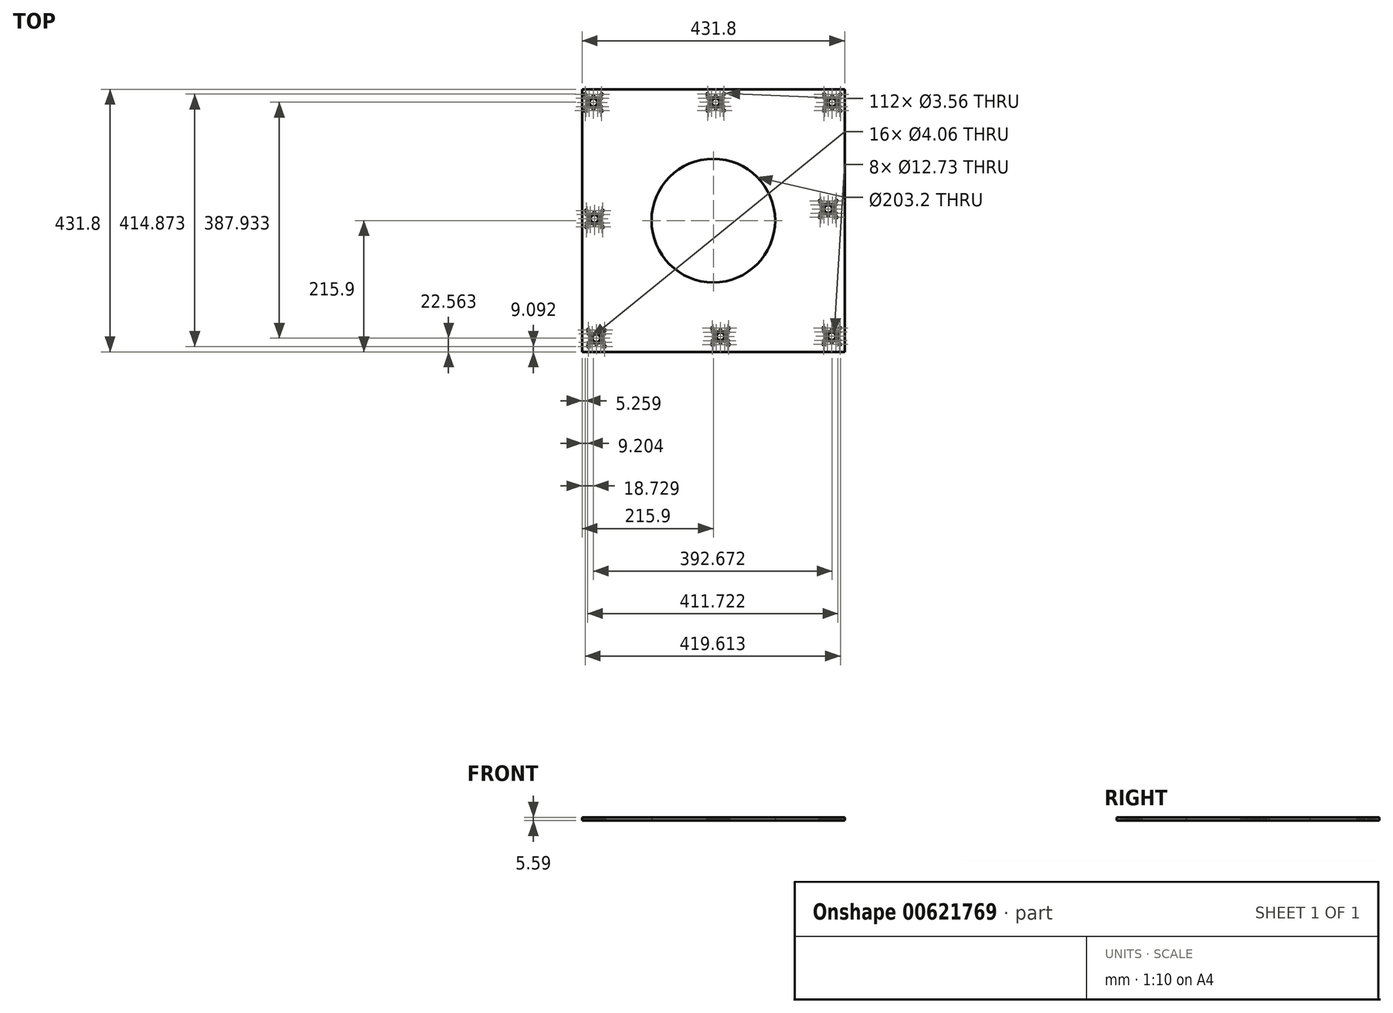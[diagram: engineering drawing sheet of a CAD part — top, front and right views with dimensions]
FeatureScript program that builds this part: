
annotation { "Feature Type Name" : "Feature", "Feature Type Description" : "" }
export const myFeature = defineFeature(function(context is Context, id is Id, definition is map)
    precondition{}
    {
        {
            var Q0;
            Q0=qCreatedBy(makeId("Top.planeOp"),FACE);
            var sketch = newSketch(context, id + "F0", { "sketchPlane" : qUnion([Q0])});
            skLineSegment(sketch, "E0.bottom", {"start": v(215.9, 215.9) * mm, "end": v(-215.9, 215.9) * mm});
            skLineSegment(sketch, "E0.top", {"start": v(215.9, -215.9) * mm, "end": v(-215.9, -215.9) * mm});
            skLineSegment(sketch, "E0.left", {"start": v(215.9, 215.9) * mm, "end": v(215.9, -215.9) * mm});
            skLineSegment(sketch, "E0.right", {"start": v(-215.9, 215.9) * mm, "end": v(-215.9, -215.9) * mm});
            skPoint(sketch, "E0.middle", {"position": v(0, 0) * mm});
            skCircle(sketch, "E1", {"center": v(-197.17, 203.97) * mm, "radius": 1.78 * mm});
            skPoint(sketch, "E1.first.point", {"position": v(-197.12, 205.75) * mm});
            skPoint(sketch, "E1.second.point", {"position": v(-196.95, 202.2) * mm});
            skPoint(sketch, "E1.third.point", {"position": v(-198.95, 203.93) * mm});
            skCircle(sketch, "E2", {"center": v(-197.17, 184.41) * mm, "radius": 1.78 * mm});
            skPoint(sketch, "E2.first.point", {"position": v(-197.01, 182.64) * mm});
            skPoint(sketch, "E2.second.point", {"position": v(-195.97, 185.72) * mm});
            skPoint(sketch, "E2.third.point", {"position": v(-197.85, 186.05) * mm});
            skPoint(sketch, "E3.first.point", {"position": v(-203.33, 179.04) * mm});
            skPoint(sketch, "E3.second.point", {"position": v(-201.5, 181.99) * mm});
            skPoint(sketch, "E3.third.point", {"position": v(-204.3, 181.6) * mm});
            skPoint(sketch, "E4.first.point", {"position": v(-190.35, 179.44) * mm});
            skPoint(sketch, "E4.second.point", {"position": v(-191.53, 182.5) * mm});
            skPoint(sketch, "E4.third.point", {"position": v(-193.13, 179.84) * mm});
            skPoint(sketch, "E5.first.point", {"position": v(-191.34, 205.9) * mm});
            skPoint(sketch, "E5.second.point", {"position": v(-191.37, 209.42) * mm});
            skPoint(sketch, "E5.third.point", {"position": v(-193.33, 207.3) * mm});
            skPoint(sketch, "E6.first.point", {"position": v(-204.43, 207.08) * mm});
            skPoint(sketch, "E6.second.point", {"position": v(-201.44, 208.86) * mm});
            skPoint(sketch, "E6.third.point", {"position": v(-203.63, 209.2) * mm});
            skCircle(sketch, "E7", {"center": v(-210.64, 207.66) * mm, "radius": 1.78 * mm});
            skPoint(sketch, "E7.first.point", {"position": v(-210.57, 209.44) * mm});
            skPoint(sketch, "E7.second.point", {"position": v(-209.71, 206.14) * mm});
            skPoint(sketch, "E7.third.point", {"position": v(-212.15, 206.72) * mm});
            skCircle(sketch, "E8", {"center": v(-183.7, 207.66) * mm, "radius": 1.78 * mm});
            skPoint(sketch, "E8.first.point", {"position": v(-183.2, 205.95) * mm});
            skPoint(sketch, "E8.second.point", {"position": v(-183.5, 209.43) * mm});
            skPoint(sketch, "E8.third.point", {"position": v(-185.46, 207.43) * mm});
            skCircle(sketch, "E9", {"center": v(-185.04, 201.1) * mm, "radius": 1.78 * mm});
            skPoint(sketch, "E9.first.point", {"position": v(-184.76, 202.86) * mm});
            skPoint(sketch, "E9.second.point", {"position": v(-185, 199.33) * mm});
            skPoint(sketch, "E9.third.point", {"position": v(-186, 202.6) * mm});
            skCircle(sketch, "E10", {"center": v(-190.26, 201.1) * mm, "radius": 1.78 * mm});
            skPoint(sketch, "E10.first.point", {"position": v(-189.77, 199.4) * mm});
            skPoint(sketch, "E10.second.point", {"position": v(-190.12, 202.88) * mm});
            skPoint(sketch, "E10.third.point", {"position": v(-191.55, 202.32) * mm});
            skCircle(sketch, "E11", {"center": v(-204.09, 201.1) * mm, "radius": 1.78 * mm});
            skPoint(sketch, "E11.first.point", {"position": v(-204.41, 199.36) * mm});
            skPoint(sketch, "E11.second.point", {"position": v(-202.41, 201.7) * mm});
            skPoint(sketch, "E11.third.point", {"position": v(-204.37, 202.86) * mm});
            skCircle(sketch, "E12", {"center": v(-209.3, 201.1) * mm, "radius": 1.78 * mm});
            skPoint(sketch, "E12.first.point", {"position": v(-209.27, 199.33) * mm});
            skPoint(sketch, "E12.second.point", {"position": v(-208.54, 202.7) * mm});
            skPoint(sketch, "E12.third.point", {"position": v(-209.18, 202.88) * mm});
            skCircle(sketch, "E13", {"center": v(-206.7, 194.19) * mm, "radius": 2.03 * mm});
            skPoint(sketch, "E13.first.point", {"position": v(-205.34, 195.7) * mm});
            skPoint(sketch, "E13.second.point", {"position": v(-205.21, 192.8) * mm});
            skPoint(sketch, "E13.third.point", {"position": v(-208.45, 195.21) * mm});
            skCircle(sketch, "E14", {"center": v(-197.17, 194.19) * mm, "radius": 6.36 * mm});
            skPoint(sketch, "E14.first.point", {"position": v(-198.39, 187.94) * mm});
            skPoint(sketch, "E14.second.point", {"position": v(-191.45, 196.97) * mm});
            skPoint(sketch, "E14.third.point", {"position": v(-201.2, 199.12) * mm});
            skCircle(sketch, "E15", {"center": v(-187.65, 194.19) * mm, "radius": 2.03 * mm});
            skPoint(sketch, "E15.first.point", {"position": v(-187.5, 192.16) * mm});
            skPoint(sketch, "E15.second.point", {"position": v(-186.02, 195.4) * mm});
            skPoint(sketch, "E15.third.point", {"position": v(-188.05, 196.18) * mm});
            skCircle(sketch, "E16", {"center": v(-185.04, 187.27) * mm, "radius": 1.78 * mm});
            skPoint(sketch, "E16.first.point", {"position": v(-184.91, 185.5) * mm});
            skPoint(sketch, "E16.second.point", {"position": v(-183.5, 188.16) * mm});
            skPoint(sketch, "E16.third.point", {"position": v(-186.23, 188.6) * mm});
            skCircle(sketch, "E17", {"center": v(-190.26, 187.27) * mm, "radius": 1.78 * mm});
            skPoint(sketch, "E17.first.point", {"position": v(-190.37, 185.5) * mm});
            skPoint(sketch, "E17.second.point", {"position": v(-189.35, 188.8) * mm});
            skPoint(sketch, "E17.third.point", {"position": v(-191.13, 188.82) * mm});
            skCircle(sketch, "E18", {"center": v(-183.7, 180.72) * mm, "radius": 1.78 * mm});
            skPoint(sketch, "E18.first.point", {"position": v(-184.91, 179.42) * mm});
            skPoint(sketch, "E18.second.point", {"position": v(-182.65, 182.16) * mm});
            skPoint(sketch, "E18.third.point", {"position": v(-182.59, 179.33) * mm});
            skCircle(sketch, "E19", {"center": v(-210.64, 180.72) * mm, "radius": 1.78 * mm});
            skPoint(sketch, "E19.first.point", {"position": v(-211.22, 179.04) * mm});
            skPoint(sketch, "E19.second.point", {"position": v(-209.26, 181.84) * mm});
            skPoint(sketch, "E19.third.point", {"position": v(-211.92, 181.96) * mm});
            skCircle(sketch, "E20", {"center": v(-209.3, 187.27) * mm, "radius": 1.78 * mm});
            skPoint(sketch, "E20.first.point", {"position": v(-209.7, 185.54) * mm});
            skPoint(sketch, "E20.second.point", {"position": v(-208.08, 188.56) * mm});
            skPoint(sketch, "E20.third.point", {"position": v(-209.79, 188.99) * mm});
            skCircle(sketch, "E21", {"center": v(-204.09, 187.27) * mm, "radius": 1.78 * mm});
            skPoint(sketch, "E21.first.point", {"position": v(-204.51, 185.55) * mm});
            skPoint(sketch, "E21.second.point", {"position": v(-203.33, 188.88) * mm});
            skPoint(sketch, "E21.third.point", {"position": v(-205.24, 188.62) * mm});
            skCircle(sketch, "E22", {"center": v(195.5, 203.97) * mm, "radius": 1.78 * mm});
            skPoint(sketch, "E22.first.point", {"position": v(195.55, 205.75) * mm});
            skPoint(sketch, "E22.second.point", {"position": v(195.72, 202.2) * mm});
            skPoint(sketch, "E22.third.point", {"position": v(193.72, 203.93) * mm});
            skCircle(sketch, "E23", {"center": v(195.5, 184.41) * mm, "radius": 1.78 * mm});
            skPoint(sketch, "E23.first.point", {"position": v(195.66, 182.64) * mm});
            skPoint(sketch, "E23.second.point", {"position": v(196.7, 185.72) * mm});
            skPoint(sketch, "E23.third.point", {"position": v(194.82, 186.05) * mm});
            skPoint(sketch, "E24.first.point", {"position": v(189.34, 179.04) * mm});
            skPoint(sketch, "E24.second.point", {"position": v(191.17, 181.99) * mm});
            skPoint(sketch, "E24.third.point", {"position": v(188.38, 181.6) * mm});
            skPoint(sketch, "E25.first.point", {"position": v(202.32, 179.44) * mm});
            skPoint(sketch, "E25.second.point", {"position": v(201.14, 182.5) * mm});
            skPoint(sketch, "E25.third.point", {"position": v(199.54, 179.84) * mm});
            skPoint(sketch, "E26.first.point", {"position": v(201.33, 205.9) * mm});
            skPoint(sketch, "E26.second.point", {"position": v(201.3, 209.42) * mm});
            skPoint(sketch, "E26.third.point", {"position": v(199.34, 207.3) * mm});
            skPoint(sketch, "E27.first.point", {"position": v(188.24, 207.08) * mm});
            skPoint(sketch, "E27.second.point", {"position": v(191.23, 208.86) * mm});
            skPoint(sketch, "E27.third.point", {"position": v(189.04, 209.2) * mm});
            skCircle(sketch, "E28", {"center": v(182.03, 207.66) * mm, "radius": 1.78 * mm});
            skPoint(sketch, "E28.first.point", {"position": v(182.1, 209.44) * mm});
            skPoint(sketch, "E28.second.point", {"position": v(182.96, 206.14) * mm});
            skPoint(sketch, "E28.third.point", {"position": v(180.52, 206.72) * mm});
            skCircle(sketch, "E29", {"center": v(208.97, 207.66) * mm, "radius": 1.78 * mm});
            skPoint(sketch, "E29.first.point", {"position": v(209.47, 205.95) * mm});
            skPoint(sketch, "E29.second.point", {"position": v(209.18, 209.43) * mm});
            skPoint(sketch, "E29.third.point", {"position": v(207.2, 207.43) * mm});
            skCircle(sketch, "E30", {"center": v(207.64, 201.1) * mm, "radius": 1.78 * mm});
            skPoint(sketch, "E30.first.point", {"position": v(207.92, 202.86) * mm});
            skPoint(sketch, "E30.second.point", {"position": v(207.67, 199.33) * mm});
            skPoint(sketch, "E30.third.point", {"position": v(206.66, 202.6) * mm});
            skCircle(sketch, "E31", {"center": v(202.42, 201.1) * mm, "radius": 1.78 * mm});
            skPoint(sketch, "E31.first.point", {"position": v(202.9, 199.4) * mm});
            skPoint(sketch, "E31.second.point", {"position": v(202.56, 202.88) * mm});
            skPoint(sketch, "E31.third.point", {"position": v(201.12, 202.32) * mm});
            skCircle(sketch, "E32", {"center": v(188.59, 201.1) * mm, "radius": 1.78 * mm});
            skPoint(sketch, "E32.first.point", {"position": v(188.26, 199.36) * mm});
            skPoint(sketch, "E32.second.point", {"position": v(190.26, 201.7) * mm});
            skPoint(sketch, "E32.third.point", {"position": v(188.3, 202.86) * mm});
            skCircle(sketch, "E33", {"center": v(183.37, 201.1) * mm, "radius": 1.78 * mm});
            skPoint(sketch, "E33.first.point", {"position": v(183.4, 199.33) * mm});
            skPoint(sketch, "E33.second.point", {"position": v(184.14, 202.7) * mm});
            skPoint(sketch, "E33.third.point", {"position": v(183.49, 202.88) * mm});
            skCircle(sketch, "E34", {"center": v(185.98, 194.19) * mm, "radius": 2.03 * mm});
            skPoint(sketch, "E34.first.point", {"position": v(187.34, 195.7) * mm});
            skPoint(sketch, "E34.second.point", {"position": v(187.46, 192.8) * mm});
            skPoint(sketch, "E34.third.point", {"position": v(184.22, 195.21) * mm});
            skCircle(sketch, "E35", {"center": v(195.5, 194.19) * mm, "radius": 6.36 * mm});
            skPoint(sketch, "E35.first.point", {"position": v(194.29, 187.94) * mm});
            skPoint(sketch, "E35.second.point", {"position": v(201.22, 196.97) * mm});
            skPoint(sketch, "E35.third.point", {"position": v(191.48, 199.12) * mm});
            skCircle(sketch, "E36", {"center": v(205.03, 194.19) * mm, "radius": 2.03 * mm});
            skPoint(sketch, "E36.first.point", {"position": v(205.17, 192.16) * mm});
            skPoint(sketch, "E36.second.point", {"position": v(206.65, 195.4) * mm});
            skPoint(sketch, "E36.third.point", {"position": v(204.62, 196.18) * mm});
            skCircle(sketch, "E37", {"center": v(207.64, 187.27) * mm, "radius": 1.78 * mm});
            skPoint(sketch, "E37.first.point", {"position": v(207.76, 185.5) * mm});
            skPoint(sketch, "E37.second.point", {"position": v(209.18, 188.16) * mm});
            skPoint(sketch, "E37.third.point", {"position": v(206.44, 188.6) * mm});
            skCircle(sketch, "E38", {"center": v(202.42, 187.27) * mm, "radius": 1.78 * mm});
            skPoint(sketch, "E38.first.point", {"position": v(202.3, 185.5) * mm});
            skPoint(sketch, "E38.second.point", {"position": v(203.33, 188.8) * mm});
            skPoint(sketch, "E38.third.point", {"position": v(201.54, 188.82) * mm});
            skCircle(sketch, "E39", {"center": v(208.97, 180.72) * mm, "radius": 1.78 * mm});
            skPoint(sketch, "E39.first.point", {"position": v(207.76, 179.42) * mm});
            skPoint(sketch, "E39.second.point", {"position": v(210.02, 182.16) * mm});
            skPoint(sketch, "E39.third.point", {"position": v(210.09, 179.33) * mm});
            skCircle(sketch, "E40", {"center": v(182.03, 180.72) * mm, "radius": 1.78 * mm});
            skPoint(sketch, "E40.first.point", {"position": v(181.45, 179.04) * mm});
            skPoint(sketch, "E40.second.point", {"position": v(183.41, 181.84) * mm});
            skPoint(sketch, "E40.third.point", {"position": v(180.76, 181.96) * mm});
            skCircle(sketch, "E41", {"center": v(183.37, 187.27) * mm, "radius": 1.78 * mm});
            skPoint(sketch, "E41.first.point", {"position": v(182.97, 185.54) * mm});
            skPoint(sketch, "E41.second.point", {"position": v(184.6, 188.56) * mm});
            skPoint(sketch, "E41.third.point", {"position": v(182.88, 188.99) * mm});
            skCircle(sketch, "E42", {"center": v(188.59, 187.27) * mm, "radius": 1.78 * mm});
            skPoint(sketch, "E42.first.point", {"position": v(188.16, 185.55) * mm});
            skPoint(sketch, "E42.second.point", {"position": v(189.34, 188.88) * mm});
            skPoint(sketch, "E42.third.point", {"position": v(187.43, 188.62) * mm});
            skCircle(sketch, "E43", {"center": v(3.89, 204.37) * mm, "radius": 1.78 * mm});
            skPoint(sketch, "E43.first.point", {"position": v(3.94, 206.15) * mm});
            skPoint(sketch, "E43.second.point", {"position": v(4.11, 202.6) * mm});
            skPoint(sketch, "E43.third.point", {"position": v(2.11, 204.33) * mm});
            skCircle(sketch, "E44", {"center": v(3.89, 184.82) * mm, "radius": 1.78 * mm});
            skPoint(sketch, "E44.first.point", {"position": v(4.05, 183.05) * mm});
            skPoint(sketch, "E44.second.point", {"position": v(5.1, 186.12) * mm});
            skPoint(sketch, "E44.third.point", {"position": v(3.2, 186.46) * mm});
            skPoint(sketch, "E45.first.point", {"position": v(-2.27, 179.44) * mm});
            skPoint(sketch, "E45.second.point", {"position": v(-0.45, 182.4) * mm});
            skPoint(sketch, "E45.third.point", {"position": v(-3.24, 182) * mm});
            skPoint(sketch, "E46.first.point", {"position": v(10.7, 179.85) * mm});
            skPoint(sketch, "E46.second.point", {"position": v(9.53, 182.9) * mm});
            skPoint(sketch, "E46.third.point", {"position": v(7.93, 180.24) * mm});
            skPoint(sketch, "E47.first.point", {"position": v(9.72, 206.3) * mm});
            skPoint(sketch, "E47.second.point", {"position": v(9.69, 209.83) * mm});
            skPoint(sketch, "E47.third.point", {"position": v(7.73, 207.7) * mm});
            skPoint(sketch, "E48.first.point", {"position": v(-3.37, 207.49) * mm});
            skPoint(sketch, "E48.second.point", {"position": v(-0.38, 209.27) * mm});
            skPoint(sketch, "E48.third.point", {"position": v(-2.57, 209.6) * mm});
            skCircle(sketch, "E49", {"center": v(-9.58, 208.07) * mm, "radius": 1.78 * mm});
            skPoint(sketch, "E49.first.point", {"position": v(-9.5, 209.84) * mm});
            skPoint(sketch, "E49.second.point", {"position": v(-8.65, 206.55) * mm});
            skPoint(sketch, "E49.third.point", {"position": v(-11.1, 207.13) * mm});
            skCircle(sketch, "E50", {"center": v(17.36, 208.07) * mm, "radius": 1.78 * mm});
            skPoint(sketch, "E50.first.point", {"position": v(17.86, 206.36) * mm});
            skPoint(sketch, "E50.second.point", {"position": v(17.56, 209.83) * mm});
            skPoint(sketch, "E50.third.point", {"position": v(15.6, 207.84) * mm});
            skCircle(sketch, "E51", {"center": v(16.02, 201.5) * mm, "radius": 1.78 * mm});
            skPoint(sketch, "E51.first.point", {"position": v(16.3, 203.27) * mm});
            skPoint(sketch, "E51.second.point", {"position": v(16.06, 199.73) * mm});
            skPoint(sketch, "E51.third.point", {"position": v(15.05, 203) * mm});
            skCircle(sketch, "E52", {"center": v(10.8, 201.5) * mm, "radius": 1.78 * mm});
            skPoint(sketch, "E52.first.point", {"position": v(11.3, 199.8) * mm});
            skPoint(sketch, "E52.second.point", {"position": v(10.94, 203.28) * mm});
            skPoint(sketch, "E52.third.point", {"position": v(9.51, 202.73) * mm});
            skCircle(sketch, "E53", {"center": v(-3.03, 201.5) * mm, "radius": 1.78 * mm});
            skPoint(sketch, "E53.first.point", {"position": v(-3.35, 199.76) * mm});
            skPoint(sketch, "E53.second.point", {"position": v(-1.35, 202.11) * mm});
            skPoint(sketch, "E53.third.point", {"position": v(-3.3, 203.27) * mm});
            skCircle(sketch, "E54", {"center": v(-8.25, 201.5) * mm, "radius": 1.78 * mm});
            skPoint(sketch, "E54.first.point", {"position": v(-8.21, 199.73) * mm});
            skPoint(sketch, "E54.second.point", {"position": v(-7.47, 203.11) * mm});
            skPoint(sketch, "E54.third.point", {"position": v(-8.12, 203.28) * mm});
            skCircle(sketch, "E55", {"center": v(-5.64, 194.6) * mm, "radius": 2.03 * mm});
            skPoint(sketch, "E55.first.point", {"position": v(-4.28, 196.1) * mm});
            skPoint(sketch, "E55.second.point", {"position": v(-4.15, 193.2) * mm});
            skPoint(sketch, "E55.third.point", {"position": v(-7.4, 195.62) * mm});
            skCircle(sketch, "E56", {"center": v(3.89, 194.6) * mm, "radius": 6.36 * mm});
            skPoint(sketch, "E56.first.point", {"position": v(2.67, 188.35) * mm});
            skPoint(sketch, "E56.second.point", {"position": v(9.61, 197.38) * mm});
            skPoint(sketch, "E56.third.point", {"position": v(-0.13, 199.53) * mm});
            skCircle(sketch, "E57", {"center": v(13.41, 194.6) * mm, "radius": 2.03 * mm});
            skPoint(sketch, "E57.first.point", {"position": v(13.56, 192.57) * mm});
            skPoint(sketch, "E57.second.point", {"position": v(15.04, 195.81) * mm});
            skPoint(sketch, "E57.third.point", {"position": v(13.01, 196.59) * mm});
            skCircle(sketch, "E58", {"center": v(16.02, 187.68) * mm, "radius": 1.78 * mm});
            skPoint(sketch, "E58.first.point", {"position": v(16.15, 185.9) * mm});
            skPoint(sketch, "E58.second.point", {"position": v(17.57, 188.56) * mm});
            skPoint(sketch, "E58.third.point", {"position": v(14.83, 189) * mm});
            skCircle(sketch, "E59", {"center": v(10.8, 187.68) * mm, "radius": 1.78 * mm});
            skPoint(sketch, "E59.first.point", {"position": v(10.7, 185.9) * mm});
            skPoint(sketch, "E59.second.point", {"position": v(11.71, 189.2) * mm});
            skPoint(sketch, "E59.third.point", {"position": v(9.93, 189.23) * mm});
            skCircle(sketch, "E60", {"center": v(17.36, 181.12) * mm, "radius": 1.78 * mm});
            skPoint(sketch, "E60.first.point", {"position": v(16.15, 179.82) * mm});
            skPoint(sketch, "E60.second.point", {"position": v(18.4, 182.56) * mm});
            skPoint(sketch, "E60.third.point", {"position": v(18.47, 179.74) * mm});
            skCircle(sketch, "E61", {"center": v(-9.58, 181.12) * mm, "radius": 1.78 * mm});
            skPoint(sketch, "E61.first.point", {"position": v(-10.16, 179.44) * mm});
            skPoint(sketch, "E61.second.point", {"position": v(-8.2, 182.24) * mm});
            skPoint(sketch, "E61.third.point", {"position": v(-10.86, 182.36) * mm});
            skCircle(sketch, "E62", {"center": v(-8.25, 187.68) * mm, "radius": 1.78 * mm});
            skPoint(sketch, "E62.first.point", {"position": v(-8.65, 185.95) * mm});
            skPoint(sketch, "E62.second.point", {"position": v(-7.02, 188.97) * mm});
            skPoint(sketch, "E62.third.point", {"position": v(-8.73, 189.4) * mm});
            skCircle(sketch, "E63", {"center": v(-3.03, 187.68) * mm, "radius": 1.78 * mm});
            skPoint(sketch, "E63.first.point", {"position": v(-3.45, 185.95) * mm});
            skPoint(sketch, "E63.second.point", {"position": v(-2.27, 189.29) * mm});
            skPoint(sketch, "E63.third.point", {"position": v(-4.18, 189.03) * mm});
            skCircle(sketch, "E64", {"center": v(-195.44, 12.79) * mm, "radius": 1.78 * mm});
            skPoint(sketch, "E64.first.point", {"position": v(-195.39, 14.57) * mm});
            skPoint(sketch, "E64.second.point", {"position": v(-195.22, 11.02) * mm});
            skPoint(sketch, "E64.third.point", {"position": v(-197.22, 12.75) * mm});
            skCircle(sketch, "E65", {"center": v(-195.44, -6.77) * mm, "radius": 1.78 * mm});
            skPoint(sketch, "E65.first.point", {"position": v(-195.28, -8.54) * mm});
            skPoint(sketch, "E65.second.point", {"position": v(-194.24, -5.46) * mm});
            skPoint(sketch, "E65.third.point", {"position": v(-196.12, -5.13) * mm});
            skPoint(sketch, "E66.first.point", {"position": v(-201.6, -12.14) * mm});
            skPoint(sketch, "E66.second.point", {"position": v(-199.78, -9.2) * mm});
            skPoint(sketch, "E66.third.point", {"position": v(-202.57, -9.58) * mm});
            skPoint(sketch, "E67.first.point", {"position": v(-188.62, -11.74) * mm});
            skPoint(sketch, "E67.second.point", {"position": v(-189.8, -8.68) * mm});
            skPoint(sketch, "E67.third.point", {"position": v(-191.4, -11.34) * mm});
            skPoint(sketch, "E68.first.point", {"position": v(-189.6, 14.72) * mm});
            skPoint(sketch, "E68.second.point", {"position": v(-189.64, 18.24) * mm});
            skPoint(sketch, "E68.third.point", {"position": v(-191.6, 16.12) * mm});
            skPoint(sketch, "E69.first.point", {"position": v(-202.7, 15.9) * mm});
            skPoint(sketch, "E69.second.point", {"position": v(-199.71, 17.68) * mm});
            skPoint(sketch, "E69.third.point", {"position": v(-201.9, 18.02) * mm});
            skCircle(sketch, "E70", {"center": v(-208.91, 16.48) * mm, "radius": 1.78 * mm});
            skPoint(sketch, "E70.first.point", {"position": v(-208.84, 18.26) * mm});
            skPoint(sketch, "E70.second.point", {"position": v(-207.98, 14.97) * mm});
            skPoint(sketch, "E70.third.point", {"position": v(-210.42, 15.55) * mm});
            skCircle(sketch, "E71", {"center": v(-181.97, 16.48) * mm, "radius": 1.78 * mm});
            skPoint(sketch, "E71.first.point", {"position": v(-181.47, 14.77) * mm});
            skPoint(sketch, "E71.second.point", {"position": v(-181.77, 18.25) * mm});
            skPoint(sketch, "E71.third.point", {"position": v(-183.73, 16.25) * mm});
            skCircle(sketch, "E72", {"center": v(-183.3, 9.92) * mm, "radius": 1.78 * mm});
            skPoint(sketch, "E72.first.point", {"position": v(-183.03, 11.68) * mm});
            skPoint(sketch, "E72.second.point", {"position": v(-183.27, 8.15) * mm});
            skPoint(sketch, "E72.third.point", {"position": v(-184.28, 11.41) * mm});
            skCircle(sketch, "E73", {"center": v(-188.53, 9.92) * mm, "radius": 1.78 * mm});
            skPoint(sketch, "E73.first.point", {"position": v(-188.04, 8.21) * mm});
            skPoint(sketch, "E73.second.point", {"position": v(-188.39, 11.7) * mm});
            skPoint(sketch, "E73.third.point", {"position": v(-189.82, 11.14) * mm});
            skCircle(sketch, "E74", {"center": v(-202.36, 9.92) * mm, "radius": 1.78 * mm});
            skPoint(sketch, "E74.first.point", {"position": v(-202.68, 8.18) * mm});
            skPoint(sketch, "E74.second.point", {"position": v(-200.68, 10.53) * mm});
            skPoint(sketch, "E74.third.point", {"position": v(-202.64, 11.68) * mm});
            skCircle(sketch, "E75", {"center": v(-207.58, 9.92) * mm, "radius": 1.78 * mm});
            skPoint(sketch, "E75.first.point", {"position": v(-207.54, 8.15) * mm});
            skPoint(sketch, "E75.second.point", {"position": v(-206.8, 11.53) * mm});
            skPoint(sketch, "E75.third.point", {"position": v(-207.45, 11.7) * mm});
            skCircle(sketch, "E76", {"center": v(-204.97, 3) * mm, "radius": 2.03 * mm});
            skPoint(sketch, "E76.first.point", {"position": v(-203.6, 4.52) * mm});
            skPoint(sketch, "E76.second.point", {"position": v(-203.48, 1.62) * mm});
            skPoint(sketch, "E76.third.point", {"position": v(-206.72, 4.03) * mm});
            skCircle(sketch, "E77", {"center": v(-195.44, 3) * mm, "radius": 6.36 * mm});
            skPoint(sketch, "E77.first.point", {"position": v(-196.66, -3.24) * mm});
            skPoint(sketch, "E77.second.point", {"position": v(-189.72, 5.8) * mm});
            skPoint(sketch, "E77.third.point", {"position": v(-199.46, 7.94) * mm});
            skCircle(sketch, "E78", {"center": v(-185.92, 3) * mm, "radius": 2.03 * mm});
            skPoint(sketch, "E78.first.point", {"position": v(-185.77, 0.98) * mm});
            skPoint(sketch, "E78.second.point", {"position": v(-184.29, 4.23) * mm});
            skPoint(sketch, "E78.third.point", {"position": v(-186.32, 5) * mm});
            skCircle(sketch, "E79", {"center": v(-183.3, -3.9) * mm, "radius": 1.78 * mm});
            skPoint(sketch, "E79.first.point", {"position": v(-183.18, -5.68) * mm});
            skPoint(sketch, "E79.second.point", {"position": v(-181.76, -3.02) * mm});
            skPoint(sketch, "E79.third.point", {"position": v(-184.5, -2.59) * mm});
            skCircle(sketch, "E80", {"center": v(-188.53, -3.9) * mm, "radius": 1.78 * mm});
            skPoint(sketch, "E80.first.point", {"position": v(-188.64, -5.68) * mm});
            skPoint(sketch, "E80.second.point", {"position": v(-187.62, -2.38) * mm});
            skPoint(sketch, "E80.third.point", {"position": v(-189.4, -2.36) * mm});
            skCircle(sketch, "E81", {"center": v(-181.97, -10.46) * mm, "radius": 1.78 * mm});
            skPoint(sketch, "E81.first.point", {"position": v(-183.18, -11.76) * mm});
            skPoint(sketch, "E81.second.point", {"position": v(-180.92, -9.02) * mm});
            skPoint(sketch, "E81.third.point", {"position": v(-180.86, -11.85) * mm});
            skCircle(sketch, "E82", {"center": v(-208.91, -10.46) * mm, "radius": 1.78 * mm});
            skPoint(sketch, "E82.first.point", {"position": v(-209.5, -12.14) * mm});
            skPoint(sketch, "E82.second.point", {"position": v(-207.53, -9.34) * mm});
            skPoint(sketch, "E82.third.point", {"position": v(-210.19, -9.22) * mm});
            skCircle(sketch, "E83", {"center": v(-207.58, -3.9) * mm, "radius": 1.78 * mm});
            skPoint(sketch, "E83.first.point", {"position": v(-207.98, -5.64) * mm});
            skPoint(sketch, "E83.second.point", {"position": v(-206.35, -2.62) * mm});
            skPoint(sketch, "E83.third.point", {"position": v(-208.06, -2.2) * mm});
            skCircle(sketch, "E84", {"center": v(-202.36, -3.9) * mm, "radius": 1.78 * mm});
            skPoint(sketch, "E84.first.point", {"position": v(-202.78, -5.63) * mm});
            skPoint(sketch, "E84.second.point", {"position": v(-201.6, -2.3) * mm});
            skPoint(sketch, "E84.third.point", {"position": v(-203.51, -2.56) * mm});
            skCircle(sketch, "E85", {"center": v(-192.3, -183.56) * mm, "radius": 1.78 * mm});
            skPoint(sketch, "E85.first.point", {"position": v(-192.25, -181.78) * mm});
            skPoint(sketch, "E85.second.point", {"position": v(-192.08, -185.32) * mm});
            skPoint(sketch, "E85.third.point", {"position": v(-194.08, -183.6) * mm});
            skCircle(sketch, "E86", {"center": v(-192.3, -203.12) * mm, "radius": 1.78 * mm});
            skPoint(sketch, "E86.first.point", {"position": v(-192.14, -204.89) * mm});
            skPoint(sketch, "E86.second.point", {"position": v(-191.1, -201.8) * mm});
            skPoint(sketch, "E86.third.point", {"position": v(-192.98, -201.47) * mm});
            skPoint(sketch, "E87.first.point", {"position": v(-198.46, -208.49) * mm});
            skPoint(sketch, "E87.second.point", {"position": v(-196.63, -205.54) * mm});
            skPoint(sketch, "E87.third.point", {"position": v(-199.42, -205.93) * mm});
            skPoint(sketch, "E88.first.point", {"position": v(-185.48, -208.08) * mm});
            skPoint(sketch, "E88.second.point", {"position": v(-186.66, -205.03) * mm});
            skPoint(sketch, "E88.third.point", {"position": v(-188.26, -207.7) * mm});
            skPoint(sketch, "E89.first.point", {"position": v(-186.47, -181.63) * mm});
            skPoint(sketch, "E89.second.point", {"position": v(-186.5, -178.1) * mm});
            skPoint(sketch, "E89.third.point", {"position": v(-188.46, -180.23) * mm});
            skPoint(sketch, "E90.first.point", {"position": v(-199.56, -180.45) * mm});
            skPoint(sketch, "E90.second.point", {"position": v(-196.57, -178.66) * mm});
            skPoint(sketch, "E90.third.point", {"position": v(-198.76, -178.32) * mm});
            skCircle(sketch, "E91", {"center": v(-205.77, -179.87) * mm, "radius": 1.78 * mm});
            skPoint(sketch, "E91.first.point", {"position": v(-205.7, -178.1) * mm});
            skPoint(sketch, "E91.second.point", {"position": v(-204.84, -181.38) * mm});
            skPoint(sketch, "E91.third.point", {"position": v(-207.28, -180.8) * mm});
            skCircle(sketch, "E92", {"center": v(-178.83, -179.87) * mm, "radius": 1.78 * mm});
            skPoint(sketch, "E92.first.point", {"position": v(-178.33, -181.57) * mm});
            skPoint(sketch, "E92.second.point", {"position": v(-178.62, -178.1) * mm});
            skPoint(sketch, "E92.third.point", {"position": v(-180.6, -180.1) * mm});
            skCircle(sketch, "E93", {"center": v(-180.16, -186.42) * mm, "radius": 1.78 * mm});
            skPoint(sketch, "E93.first.point", {"position": v(-179.88, -184.67) * mm});
            skPoint(sketch, "E93.second.point", {"position": v(-180.13, -188.2) * mm});
            skPoint(sketch, "E93.third.point", {"position": v(-181.14, -184.93) * mm});
            skCircle(sketch, "E94", {"center": v(-185.38, -186.42) * mm, "radius": 1.78 * mm});
            skPoint(sketch, "E94.first.point", {"position": v(-184.9, -188.13) * mm});
            skPoint(sketch, "E94.second.point", {"position": v(-185.24, -184.65) * mm});
            skPoint(sketch, "E94.third.point", {"position": v(-186.68, -185.2) * mm});
            skCircle(sketch, "E95", {"center": v(-199.21, -186.42) * mm, "radius": 1.78 * mm});
            skPoint(sketch, "E95.first.point", {"position": v(-199.54, -188.17) * mm});
            skPoint(sketch, "E95.second.point", {"position": v(-197.54, -185.82) * mm});
            skPoint(sketch, "E95.third.point", {"position": v(-199.5, -184.67) * mm});
            skCircle(sketch, "E96", {"center": v(-204.43, -186.42) * mm, "radius": 1.78 * mm});
            skPoint(sketch, "E96.first.point", {"position": v(-204.4, -188.2) * mm});
            skPoint(sketch, "E96.second.point", {"position": v(-203.66, -184.82) * mm});
            skPoint(sketch, "E96.third.point", {"position": v(-204.31, -184.65) * mm});
            skCircle(sketch, "E97", {"center": v(-201.82, -193.34) * mm, "radius": 2.03 * mm});
            skPoint(sketch, "E97.first.point", {"position": v(-200.46, -191.83) * mm});
            skPoint(sketch, "E97.second.point", {"position": v(-200.34, -194.72) * mm});
            skPoint(sketch, "E97.third.point", {"position": v(-203.58, -192.31) * mm});
            skCircle(sketch, "E98", {"center": v(-192.3, -193.34) * mm, "radius": 6.36 * mm});
            skPoint(sketch, "E98.first.point", {"position": v(-193.51, -199.58) * mm});
            skPoint(sketch, "E98.second.point", {"position": v(-186.58, -190.56) * mm});
            skPoint(sketch, "E98.third.point", {"position": v(-196.32, -188.4) * mm});
            skCircle(sketch, "E99", {"center": v(-182.77, -193.34) * mm, "radius": 2.03 * mm});
            skPoint(sketch, "E99.first.point", {"position": v(-182.63, -195.36) * mm});
            skPoint(sketch, "E99.second.point", {"position": v(-181.15, -192.12) * mm});
            skPoint(sketch, "E99.third.point", {"position": v(-183.18, -191.35) * mm});
            skCircle(sketch, "E100", {"center": v(-180.16, -200.25) * mm, "radius": 1.78 * mm});
            skPoint(sketch, "E100.first.point", {"position": v(-180.04, -202.03) * mm});
            skPoint(sketch, "E100.second.point", {"position": v(-178.62, -199.37) * mm});
            skPoint(sketch, "E100.third.point", {"position": v(-181.36, -198.93) * mm});
            skCircle(sketch, "E101", {"center": v(-185.38, -200.25) * mm, "radius": 1.78 * mm});
            skPoint(sketch, "E101.first.point", {"position": v(-185.5, -202.03) * mm});
            skPoint(sketch, "E101.second.point", {"position": v(-184.47, -198.72) * mm});
            skPoint(sketch, "E101.third.point", {"position": v(-186.26, -198.7) * mm});
            skCircle(sketch, "E102", {"center": v(-178.83, -206.8) * mm, "radius": 1.78 * mm});
            skPoint(sketch, "E102.first.point", {"position": v(-180.04, -208.1) * mm});
            skPoint(sketch, "E102.second.point", {"position": v(-177.78, -205.37) * mm});
            skPoint(sketch, "E102.third.point", {"position": v(-177.71, -208.2) * mm});
            skCircle(sketch, "E103", {"center": v(-205.77, -206.8) * mm, "radius": 1.78 * mm});
            skPoint(sketch, "E103.first.point", {"position": v(-206.35, -208.49) * mm});
            skPoint(sketch, "E103.second.point", {"position": v(-204.39, -205.7) * mm});
            skPoint(sketch, "E103.third.point", {"position": v(-207.04, -205.57) * mm});
            skCircle(sketch, "E104", {"center": v(-204.43, -200.25) * mm, "radius": 1.78 * mm});
            skPoint(sketch, "E104.first.point", {"position": v(-204.83, -201.98) * mm});
            skPoint(sketch, "E104.second.point", {"position": v(-203.2, -198.97) * mm});
            skPoint(sketch, "E104.third.point", {"position": v(-204.92, -198.54) * mm});
            skCircle(sketch, "E105", {"center": v(-199.21, -200.25) * mm, "radius": 1.78 * mm});
            skPoint(sketch, "E105.first.point", {"position": v(-199.64, -201.98) * mm});
            skPoint(sketch, "E105.second.point", {"position": v(-198.46, -198.64) * mm});
            skPoint(sketch, "E105.third.point", {"position": v(-200.37, -198.9) * mm});
            skCircle(sketch, "E106", {"center": v(11.78, -180.6) * mm, "radius": 1.78 * mm});
            skPoint(sketch, "E106.first.point", {"position": v(11.83, -178.83) * mm});
            skPoint(sketch, "E106.second.point", {"position": v(12, -182.37) * mm});
            skPoint(sketch, "E106.third.point", {"position": v(10, -180.65) * mm});
            skCircle(sketch, "E107", {"center": v(11.78, -200.17) * mm, "radius": 1.78 * mm});
            skPoint(sketch, "E107.first.point", {"position": v(11.94, -201.94) * mm});
            skPoint(sketch, "E107.second.point", {"position": v(12.99, -198.86) * mm});
            skPoint(sketch, "E107.third.point", {"position": v(11.1, -198.52) * mm});
            skPoint(sketch, "E108.first.point", {"position": v(5.62, -205.54) * mm});
            skPoint(sketch, "E108.second.point", {"position": v(7.45, -202.59) * mm});
            skPoint(sketch, "E108.third.point", {"position": v(4.65, -202.98) * mm});
            skPoint(sketch, "E109.first.point", {"position": v(18.6, -205.13) * mm});
            skPoint(sketch, "E109.second.point", {"position": v(17.42, -202.08) * mm});
            skPoint(sketch, "E109.third.point", {"position": v(15.82, -204.74) * mm});
            skPoint(sketch, "E110.first.point", {"position": v(17.61, -178.68) * mm});
            skPoint(sketch, "E110.second.point", {"position": v(17.58, -175.15) * mm});
            skPoint(sketch, "E110.third.point", {"position": v(15.62, -177.28) * mm});
            skPoint(sketch, "E111.first.point", {"position": v(4.52, -177.5) * mm});
            skPoint(sketch, "E111.second.point", {"position": v(7.5, -175.71) * mm});
            skPoint(sketch, "E111.third.point", {"position": v(5.32, -175.37) * mm});
            skCircle(sketch, "E112", {"center": v(-1.7, -176.92) * mm, "radius": 1.78 * mm});
            skPoint(sketch, "E112.first.point", {"position": v(-1.62, -175.14) * mm});
            skPoint(sketch, "E112.second.point", {"position": v(-0.76, -178.43) * mm});
            skPoint(sketch, "E112.third.point", {"position": v(-3.2, -177.85) * mm});
            skCircle(sketch, "E113", {"center": v(25.25, -176.92) * mm, "radius": 1.78 * mm});
            skPoint(sketch, "E113.first.point", {"position": v(25.75, -178.62) * mm});
            skPoint(sketch, "E113.second.point", {"position": v(25.45, -175.15) * mm});
            skPoint(sketch, "E113.third.point", {"position": v(23.49, -177.14) * mm});
            skCircle(sketch, "E114", {"center": v(23.92, -183.47) * mm, "radius": 1.78 * mm});
            skPoint(sketch, "E114.first.point", {"position": v(24.2, -181.72) * mm});
            skPoint(sketch, "E114.second.point", {"position": v(23.95, -185.25) * mm});
            skPoint(sketch, "E114.third.point", {"position": v(22.94, -181.98) * mm});
            skCircle(sketch, "E115", {"center": v(18.7, -183.47) * mm, "radius": 1.78 * mm});
            skPoint(sketch, "E115.first.point", {"position": v(19.18, -185.18) * mm});
            skPoint(sketch, "E115.second.point", {"position": v(18.84, -181.7) * mm});
            skPoint(sketch, "E115.third.point", {"position": v(17.4, -182.25) * mm});
            skCircle(sketch, "E116", {"center": v(4.87, -183.47) * mm, "radius": 1.78 * mm});
            skPoint(sketch, "E116.first.point", {"position": v(4.54, -185.22) * mm});
            skPoint(sketch, "E116.second.point", {"position": v(6.54, -182.87) * mm});
            skPoint(sketch, "E116.third.point", {"position": v(4.58, -181.72) * mm});
            skCircle(sketch, "E117", {"center": v(-0.36, -183.47) * mm, "radius": 1.78 * mm});
            skPoint(sketch, "E117.first.point", {"position": v(-0.32, -185.25) * mm});
            skPoint(sketch, "E117.second.point", {"position": v(0.42, -181.87) * mm});
            skPoint(sketch, "E117.third.point", {"position": v(-0.23, -181.7) * mm});
            skCircle(sketch, "E118", {"center": v(2.26, -190.39) * mm, "radius": 2.03 * mm});
            skPoint(sketch, "E118.first.point", {"position": v(3.62, -188.88) * mm});
            skPoint(sketch, "E118.second.point", {"position": v(3.74, -191.77) * mm});
            skPoint(sketch, "E118.third.point", {"position": v(0.5, -189.36) * mm});
            skCircle(sketch, "E119", {"center": v(11.78, -190.39) * mm, "radius": 6.36 * mm});
            skPoint(sketch, "E119.first.point", {"position": v(10.57, -196.63) * mm});
            skPoint(sketch, "E119.second.point", {"position": v(17.5, -187.6) * mm});
            skPoint(sketch, "E119.third.point", {"position": v(7.76, -185.46) * mm});
            skCircle(sketch, "E120", {"center": v(21.3, -190.39) * mm, "radius": 2.03 * mm});
            skPoint(sketch, "E120.first.point", {"position": v(21.45, -192.41) * mm});
            skPoint(sketch, "E120.second.point", {"position": v(22.93, -189.17) * mm});
            skPoint(sketch, "E120.third.point", {"position": v(20.9, -188.4) * mm});
            skCircle(sketch, "E121", {"center": v(23.92, -197.3) * mm, "radius": 1.78 * mm});
            skPoint(sketch, "E121.first.point", {"position": v(24.04, -199.08) * mm});
            skPoint(sketch, "E121.second.point", {"position": v(25.46, -196.42) * mm});
            skPoint(sketch, "E121.third.point", {"position": v(22.72, -195.98) * mm});
            skCircle(sketch, "E122", {"center": v(18.7, -197.3) * mm, "radius": 1.78 * mm});
            skPoint(sketch, "E122.first.point", {"position": v(18.58, -199.08) * mm});
            skPoint(sketch, "E122.second.point", {"position": v(19.6, -195.77) * mm});
            skPoint(sketch, "E122.third.point", {"position": v(17.82, -195.76) * mm});
            skCircle(sketch, "E123", {"center": v(25.25, -203.86) * mm, "radius": 1.78 * mm});
            skPoint(sketch, "E123.first.point", {"position": v(24.04, -205.16) * mm});
            skPoint(sketch, "E123.second.point", {"position": v(26.3, -202.42) * mm});
            skPoint(sketch, "E123.third.point", {"position": v(26.37, -205.24) * mm});
            skCircle(sketch, "E124", {"center": v(-1.7, -203.86) * mm, "radius": 1.78 * mm});
            skPoint(sketch, "E124.first.point", {"position": v(-2.27, -205.54) * mm});
            skPoint(sketch, "E124.second.point", {"position": v(-0.3, -202.74) * mm});
            skPoint(sketch, "E124.third.point", {"position": v(-2.97, -202.62) * mm});
            skCircle(sketch, "E125", {"center": v(-0.36, -197.3) * mm, "radius": 1.78 * mm});
            skPoint(sketch, "E125.first.point", {"position": v(-0.76, -199.03) * mm});
            skPoint(sketch, "E125.second.point", {"position": v(0.87, -196.02) * mm});
            skPoint(sketch, "E125.third.point", {"position": v(-0.84, -195.6) * mm});
            skCircle(sketch, "E126", {"center": v(4.87, -197.3) * mm, "radius": 1.78 * mm});
            skPoint(sketch, "E126.first.point", {"position": v(4.44, -199.03) * mm});
            skPoint(sketch, "E126.second.point", {"position": v(5.62, -195.7) * mm});
            skPoint(sketch, "E126.third.point", {"position": v(3.7, -195.95) * mm});
            skCircle(sketch, "E127", {"center": v(194.8, -180.2) * mm, "radius": 1.78 * mm});
            skPoint(sketch, "E127.first.point", {"position": v(194.86, -178.42) * mm});
            skPoint(sketch, "E127.second.point", {"position": v(195.03, -181.97) * mm});
            skPoint(sketch, "E127.third.point", {"position": v(193.03, -180.24) * mm});
            skCircle(sketch, "E128", {"center": v(194.8, -199.76) * mm, "radius": 1.78 * mm});
            skPoint(sketch, "E128.first.point", {"position": v(194.96, -201.53) * mm});
            skPoint(sketch, "E128.second.point", {"position": v(196.01, -198.45) * mm});
            skPoint(sketch, "E128.third.point", {"position": v(194.12, -198.12) * mm});
            skPoint(sketch, "E129.first.point", {"position": v(188.65, -205.13) * mm});
            skPoint(sketch, "E129.second.point", {"position": v(190.47, -202.18) * mm});
            skPoint(sketch, "E129.third.point", {"position": v(187.68, -202.57) * mm});
            skPoint(sketch, "E130.first.point", {"position": v(201.62, -204.73) * mm});
            skPoint(sketch, "E130.second.point", {"position": v(200.44, -201.67) * mm});
            skPoint(sketch, "E130.third.point", {"position": v(198.84, -204.33) * mm});
            skPoint(sketch, "E131.first.point", {"position": v(200.64, -178.27) * mm});
            skPoint(sketch, "E131.second.point", {"position": v(200.6, -174.75) * mm});
            skPoint(sketch, "E131.third.point", {"position": v(198.64, -176.87) * mm});
            skPoint(sketch, "E132.first.point", {"position": v(187.54, -177.1) * mm});
            skPoint(sketch, "E132.second.point", {"position": v(190.53, -175.3) * mm});
            skPoint(sketch, "E132.third.point", {"position": v(188.34, -174.97) * mm});
            skCircle(sketch, "E133", {"center": v(181.33, -176.51) * mm, "radius": 1.78 * mm});
            skPoint(sketch, "E133.first.point", {"position": v(181.4, -174.73) * mm});
            skPoint(sketch, "E133.second.point", {"position": v(182.27, -178.03) * mm});
            skPoint(sketch, "E133.third.point", {"position": v(179.82, -177.45) * mm});
            skCircle(sketch, "E134", {"center": v(208.28, -176.51) * mm, "radius": 1.78 * mm});
            skPoint(sketch, "E134.first.point", {"position": v(208.77, -178.22) * mm});
            skPoint(sketch, "E134.second.point", {"position": v(208.48, -174.74) * mm});
            skPoint(sketch, "E134.third.point", {"position": v(206.51, -176.74) * mm});
            skCircle(sketch, "E135", {"center": v(206.94, -183.07) * mm, "radius": 1.78 * mm});
            skPoint(sketch, "E135.first.point", {"position": v(207.22, -181.31) * mm});
            skPoint(sketch, "E135.second.point", {"position": v(206.97, -184.84) * mm});
            skPoint(sketch, "E135.third.point", {"position": v(205.97, -181.58) * mm});
            skCircle(sketch, "E136", {"center": v(201.72, -183.07) * mm, "radius": 1.78 * mm});
            skPoint(sketch, "E136.first.point", {"position": v(202.2, -184.78) * mm});
            skPoint(sketch, "E136.second.point", {"position": v(201.86, -181.3) * mm});
            skPoint(sketch, "E136.third.point", {"position": v(200.43, -181.85) * mm});
            skCircle(sketch, "E137", {"center": v(187.9, -183.07) * mm, "radius": 1.78 * mm});
            skPoint(sketch, "E137.first.point", {"position": v(187.57, -184.81) * mm});
            skPoint(sketch, "E137.second.point", {"position": v(189.56, -182.46) * mm});
            skPoint(sketch, "E137.third.point", {"position": v(187.6, -181.31) * mm});
            skCircle(sketch, "E138", {"center": v(182.67, -183.07) * mm, "radius": 1.78 * mm});
            skPoint(sketch, "E138.first.point", {"position": v(182.7, -184.84) * mm});
            skPoint(sketch, "E138.second.point", {"position": v(183.44, -181.46) * mm});
            skPoint(sketch, "E138.third.point", {"position": v(182.8, -181.3) * mm});
            skCircle(sketch, "E139", {"center": v(185.28, -189.98) * mm, "radius": 2.03 * mm});
            skPoint(sketch, "E139.first.point", {"position": v(186.64, -188.47) * mm});
            skPoint(sketch, "E139.second.point", {"position": v(186.77, -191.37) * mm});
            skPoint(sketch, "E139.third.point", {"position": v(183.52, -188.96) * mm});
            skCircle(sketch, "E140", {"center": v(194.8, -189.98) * mm, "radius": 6.36 * mm});
            skPoint(sketch, "E140.first.point", {"position": v(193.59, -196.23) * mm});
            skPoint(sketch, "E140.second.point", {"position": v(200.53, -187.2) * mm});
            skPoint(sketch, "E140.third.point", {"position": v(190.78, -185.05) * mm});
            skCircle(sketch, "E141", {"center": v(204.33, -189.98) * mm, "radius": 2.03 * mm});
            skPoint(sketch, "E141.first.point", {"position": v(204.47, -192) * mm});
            skPoint(sketch, "E141.second.point", {"position": v(205.96, -188.76) * mm});
            skPoint(sketch, "E141.third.point", {"position": v(203.93, -187.99) * mm});
            skCircle(sketch, "E142", {"center": v(206.94, -196.9) * mm, "radius": 1.78 * mm});
            skPoint(sketch, "E142.first.point", {"position": v(207.06, -198.67) * mm});
            skPoint(sketch, "E142.second.point", {"position": v(208.48, -196.01) * mm});
            skPoint(sketch, "E142.third.point", {"position": v(205.75, -195.58) * mm});
            skCircle(sketch, "E143", {"center": v(201.72, -196.9) * mm, "radius": 1.78 * mm});
            skPoint(sketch, "E143.first.point", {"position": v(201.6, -198.67) * mm});
            skPoint(sketch, "E143.second.point", {"position": v(202.63, -195.37) * mm});
            skPoint(sketch, "E143.third.point", {"position": v(200.84, -195.35) * mm});
            skCircle(sketch, "E144", {"center": v(208.28, -203.45) * mm, "radius": 1.78 * mm});
            skPoint(sketch, "E144.first.point", {"position": v(207.06, -204.75) * mm});
            skPoint(sketch, "E144.second.point", {"position": v(209.32, -202.01) * mm});
            skPoint(sketch, "E144.third.point", {"position": v(209.4, -204.84) * mm});
            skCircle(sketch, "E145", {"center": v(181.33, -203.45) * mm, "radius": 1.78 * mm});
            skPoint(sketch, "E145.first.point", {"position": v(180.76, -205.13) * mm});
            skPoint(sketch, "E145.second.point", {"position": v(182.72, -202.33) * mm});
            skPoint(sketch, "E145.third.point", {"position": v(180.06, -202.21) * mm});
            skCircle(sketch, "E146", {"center": v(182.67, -196.9) * mm, "radius": 1.78 * mm});
            skPoint(sketch, "E146.first.point", {"position": v(182.27, -198.63) * mm});
            skPoint(sketch, "E146.second.point", {"position": v(183.9, -195.6) * mm});
            skPoint(sketch, "E146.third.point", {"position": v(182.19, -195.18) * mm});
            skCircle(sketch, "E147", {"center": v(187.9, -196.9) * mm, "radius": 1.78 * mm});
            skPoint(sketch, "E147.first.point", {"position": v(187.46, -198.62) * mm});
            skPoint(sketch, "E147.second.point", {"position": v(188.65, -195.29) * mm});
            skPoint(sketch, "E147.third.point", {"position": v(186.73, -195.55) * mm});
            skCircle(sketch, "E148", {"center": v(188.85, 28.87) * mm, "radius": 1.78 * mm});
            skPoint(sketch, "E148.first.point", {"position": v(188.9, 30.64) * mm});
            skPoint(sketch, "E148.second.point", {"position": v(189.07, 27.1) * mm});
            skPoint(sketch, "E148.third.point", {"position": v(187.07, 28.83) * mm});
            skCircle(sketch, "E149", {"center": v(188.85, 9.3) * mm, "radius": 1.78 * mm});
            skPoint(sketch, "E149.first.point", {"position": v(189.01, 7.54) * mm});
            skPoint(sketch, "E149.second.point", {"position": v(190.06, 10.62) * mm});
            skPoint(sketch, "E149.third.point", {"position": v(188.17, 10.95) * mm});
            skPoint(sketch, "E150.first.point", {"position": v(182.7, 3.94) * mm});
            skPoint(sketch, "E150.second.point", {"position": v(184.52, 6.89) * mm});
            skPoint(sketch, "E150.third.point", {"position": v(181.73, 6.5) * mm});
            skPoint(sketch, "E151.first.point", {"position": v(195.67, 4.34) * mm});
            skPoint(sketch, "E151.second.point", {"position": v(194.49, 7.4) * mm});
            skPoint(sketch, "E151.third.point", {"position": v(192.89, 4.73) * mm});
            skPoint(sketch, "E152.first.point", {"position": v(194.68, 30.8) * mm});
            skPoint(sketch, "E152.second.point", {"position": v(194.65, 34.32) * mm});
            skPoint(sketch, "E152.third.point", {"position": v(192.69, 32.2) * mm});
            skPoint(sketch, "E153.first.point", {"position": v(181.6, 31.98) * mm});
            skPoint(sketch, "E153.second.point", {"position": v(184.58, 33.76) * mm});
            skPoint(sketch, "E153.third.point", {"position": v(182.39, 34.1) * mm});
            skCircle(sketch, "E154", {"center": v(175.38, 32.56) * mm, "radius": 1.78 * mm});
            skPoint(sketch, "E154.first.point", {"position": v(175.45, 34.33) * mm});
            skPoint(sketch, "E154.second.point", {"position": v(176.31, 31.04) * mm});
            skPoint(sketch, "E154.third.point", {"position": v(173.87, 31.62) * mm});
            skCircle(sketch, "E155", {"center": v(202.32, 32.56) * mm, "radius": 1.78 * mm});
            skPoint(sketch, "E155.first.point", {"position": v(202.82, 30.85) * mm});
            skPoint(sketch, "E155.second.point", {"position": v(202.52, 34.32) * mm});
            skPoint(sketch, "E155.third.point", {"position": v(200.56, 32.33) * mm});
            skCircle(sketch, "E156", {"center": v(200.99, 26) * mm, "radius": 1.78 * mm});
            skPoint(sketch, "E156.first.point", {"position": v(201.27, 27.76) * mm});
            skPoint(sketch, "E156.second.point", {"position": v(201.02, 24.22) * mm});
            skPoint(sketch, "E156.third.point", {"position": v(200.01, 27.5) * mm});
            skCircle(sketch, "E157", {"center": v(195.77, 26) * mm, "radius": 1.78 * mm});
            skPoint(sketch, "E157.first.point", {"position": v(196.25, 24.3) * mm});
            skPoint(sketch, "E157.second.point", {"position": v(195.9, 27.77) * mm});
            skPoint(sketch, "E157.third.point", {"position": v(194.47, 27.22) * mm});
            skCircle(sketch, "E158", {"center": v(181.94, 26) * mm, "radius": 1.78 * mm});
            skPoint(sketch, "E158.first.point", {"position": v(181.61, 24.25) * mm});
            skPoint(sketch, "E158.second.point", {"position": v(183.6, 26.6) * mm});
            skPoint(sketch, "E158.third.point", {"position": v(181.65, 27.76) * mm});
            skCircle(sketch, "E159", {"center": v(176.72, 26) * mm, "radius": 1.78 * mm});
            skPoint(sketch, "E159.first.point", {"position": v(176.75, 24.22) * mm});
            skPoint(sketch, "E159.second.point", {"position": v(177.49, 27.6) * mm});
            skPoint(sketch, "E159.third.point", {"position": v(176.84, 27.78) * mm});
            skCircle(sketch, "E160", {"center": v(179.33, 19.09) * mm, "radius": 2.03 * mm});
            skPoint(sketch, "E160.first.point", {"position": v(180.69, 20.6) * mm});
            skPoint(sketch, "E160.second.point", {"position": v(180.81, 17.7) * mm});
            skPoint(sketch, "E160.third.point", {"position": v(177.57, 20.11) * mm});
            skCircle(sketch, "E161", {"center": v(188.85, 19.09) * mm, "radius": 6.36 * mm});
            skPoint(sketch, "E161.first.point", {"position": v(187.64, 12.84) * mm});
            skPoint(sketch, "E161.second.point", {"position": v(194.57, 21.87) * mm});
            skPoint(sketch, "E161.third.point", {"position": v(184.83, 24.02) * mm});
            skCircle(sketch, "E162", {"center": v(198.38, 19.09) * mm, "radius": 2.03 * mm});
            skPoint(sketch, "E162.first.point", {"position": v(198.52, 17.06) * mm});
            skPoint(sketch, "E162.second.point", {"position": v(200, 20.3) * mm});
            skPoint(sketch, "E162.third.point", {"position": v(197.97, 21.08) * mm});
            skCircle(sketch, "E163", {"center": v(200.99, 12.17) * mm, "radius": 1.78 * mm});
            skPoint(sketch, "E163.first.point", {"position": v(201.1, 10.4) * mm});
            skPoint(sketch, "E163.second.point", {"position": v(202.53, 13.06) * mm});
            skPoint(sketch, "E163.third.point", {"position": v(199.8, 13.5) * mm});
            skCircle(sketch, "E164", {"center": v(195.77, 12.17) * mm, "radius": 1.78 * mm});
            skPoint(sketch, "E164.first.point", {"position": v(195.65, 10.4) * mm});
            skPoint(sketch, "E164.second.point", {"position": v(196.68, 13.7) * mm});
            skPoint(sketch, "E164.third.point", {"position": v(194.89, 13.72) * mm});
            skCircle(sketch, "E165", {"center": v(202.32, 5.62) * mm, "radius": 1.78 * mm});
            skPoint(sketch, "E165.first.point", {"position": v(201.1, 4.32) * mm});
            skPoint(sketch, "E165.second.point", {"position": v(203.37, 7.05) * mm});
            skPoint(sketch, "E165.third.point", {"position": v(203.44, 4.23) * mm});
            skCircle(sketch, "E166", {"center": v(175.38, 5.62) * mm, "radius": 1.78 * mm});
            skPoint(sketch, "E166.first.point", {"position": v(174.8, 3.94) * mm});
            skPoint(sketch, "E166.second.point", {"position": v(176.76, 6.73) * mm});
            skPoint(sketch, "E166.third.point", {"position": v(174.1, 6.86) * mm});
            skCircle(sketch, "E167", {"center": v(176.72, 12.17) * mm, "radius": 1.78 * mm});
            skPoint(sketch, "E167.first.point", {"position": v(176.32, 10.44) * mm});
            skPoint(sketch, "E167.second.point", {"position": v(177.94, 13.46) * mm});
            skPoint(sketch, "E167.third.point", {"position": v(176.23, 13.88) * mm});
            skCircle(sketch, "E168", {"center": v(181.94, 12.17) * mm, "radius": 1.78 * mm});
            skPoint(sketch, "E168.first.point", {"position": v(181.5, 10.45) * mm});
            skPoint(sketch, "E168.second.point", {"position": v(182.7, 13.78) * mm});
            skPoint(sketch, "E168.third.point", {"position": v(180.78, 13.52) * mm});
            skCircle(sketch, "E169", {"center": v(0, 0) * mm, "radius": 101.6 * mm});
            skSolve(sketch);
        }
        {
            var Q0;
            Q0=makeQuery(id+"F0.imprint","IMPRINT",FACE,{"disambiguationData":[TD([[makeQuery(id+"F0.imprint","IMPRINT",EDGE,{"derivedFrom":sQuery(id+"F0.wireOp",EDGE,"E0.bottom")}),1.0]])]});
            extrude(context, id + "F1", {"entities" : qUnion([Q0]), "depth" : 5.6 * mm, "offsetDistance" : 25.4 * mm});
        }
    });
